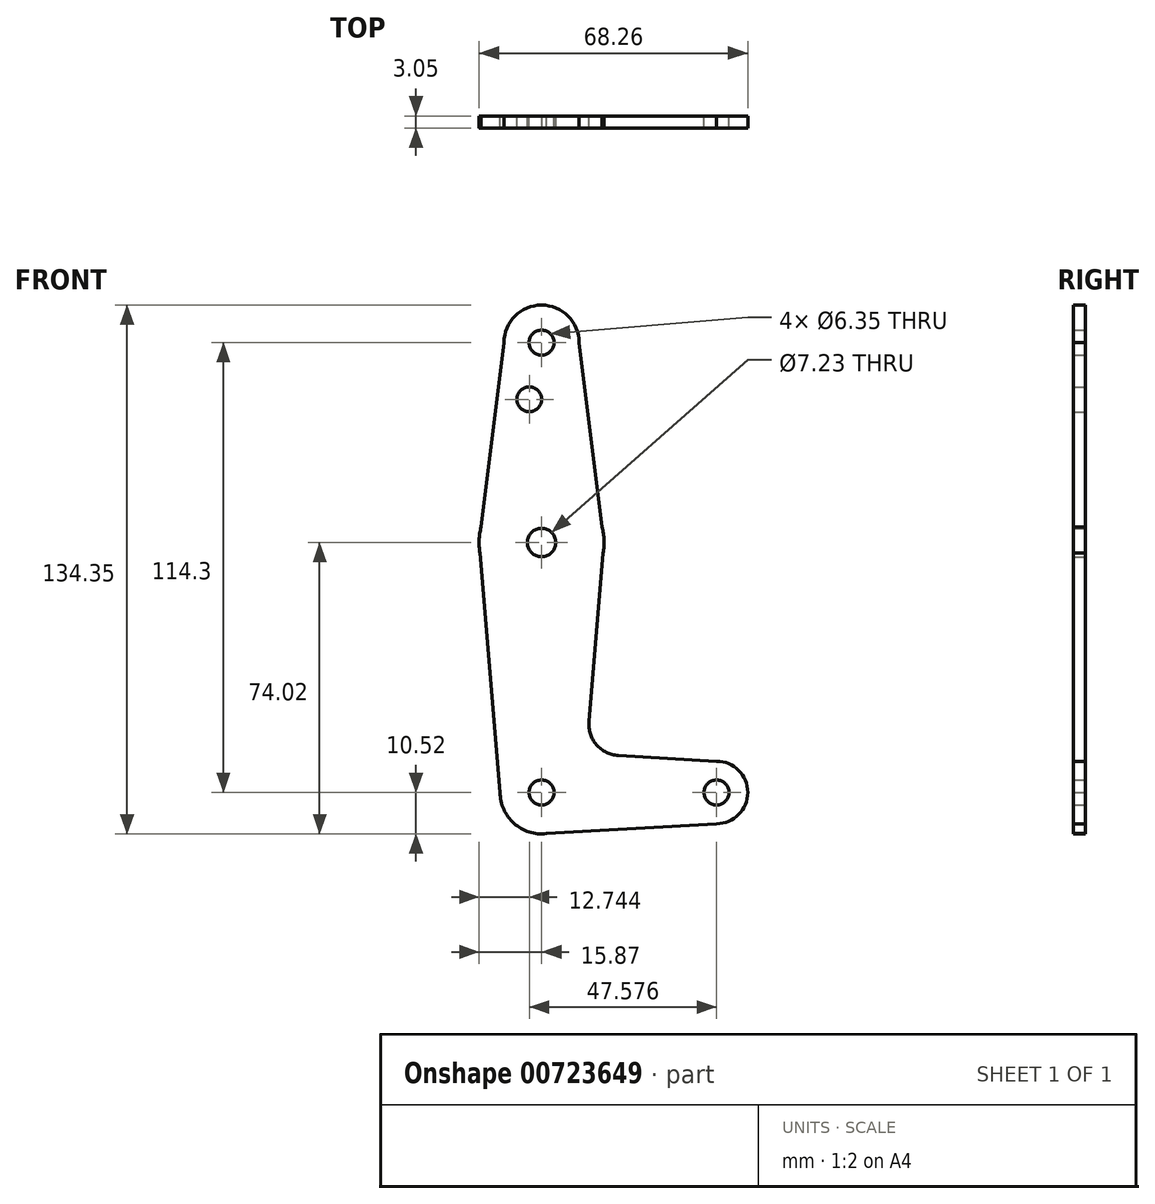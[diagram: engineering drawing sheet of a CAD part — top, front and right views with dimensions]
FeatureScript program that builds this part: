
annotation { "Feature Type Name" : "Feature", "Feature Type Description" : "" }
export const myFeature = defineFeature(function(context is Context, id is Id, definition is map)
    precondition{}
    {
        {
            var Q0;
            Q0=qCreatedBy(makeId("Front.planeOp"),FACE);
            var sketch = newSketch(context, id + "F0", { "sketchPlane" : qUnion([Q0])});
            skLineSegment(sketch, "E0", {"start": v(0, 0) * mm, "end": v(0, 114.3) * mm, "construction": true});
            skLineSegment(sketch, "E1", {"start": v(0, 0) * mm, "end": v(44.45, 0) * mm, "construction": true});
            skCircle(sketch, "E2", {"center": v(0, 114.3) * mm, "radius": 9.53 * mm});
            skCircle(sketch, "E3", {"center": v(0, 63.5) * mm, "radius": 15.88 * mm});
            skCircle(sketch, "E4", {"center": v(0, 0) * mm, "radius": 10.52 * mm});
            skCircle(sketch, "E5", {"center": v(44.45, 0) * mm, "radius": 7.94 * mm});
            skLineSegment(sketch, "E6", {"start": v(-9.53, 114.3) * mm, "end": v(-15.88, 63.5) * mm});
            skLineSegment(sketch, "E7", {"start": v(9.53, 114.3) * mm, "end": v(15.88, 63.5) * mm});
            skLineSegment(sketch, "E8", {"start": v(-10.52, 0) * mm, "end": v(-15.88, 63.5) * mm});
            skLineSegment(sketch, "E9", {"start": v(12.04, 18) * mm, "end": v(15.88, 63.5) * mm});
            skLineSegment(sketch, "E10", {"start": v(44.45, 7.94) * mm, "end": v(19.5, 9.4) * mm});
            skLineSegment(sketch, "E11", {"start": v(44.45, -7.94) * mm, "end": v(0, -10.52) * mm});
            skCircle(sketch, "E12", {"center": v(-3.13, 99.9) * mm, "radius": 3.18 * mm});
            skCircle(sketch, "E13", {"center": v(0, 114.3) * mm, "radius": 3.18 * mm});
            skCircle(sketch, "E14", {"center": v(0, 63.5) * mm, "radius": 3.62 * mm});
            skCircle(sketch, "E15", {"center": v(0, 0) * mm, "radius": 3.18 * mm});
            skCircle(sketch, "E16", {"center": v(44.45, 0) * mm, "radius": 3.18 * mm});
            skPoint(sketch, "E17.newPointB", {"position": v(0, 10.54) * mm});
            skArc(sketch, "E17.filletArc", {"start": v(12.04, 18) * mm, "mid": v(13.95, 12.13) * mm, "end": v(19.5, 9.4) * mm});
            skSolve(sketch);
        }
        {
            var Q0;
            Q0 = qSketchRegion(id + "F0", true);
            extrude(context, id + "F1", {"entities" : qUnion([Q0]), "depth" : 3.05 * mm, "offsetDistance" : 25.4 * mm});
        }
    });
